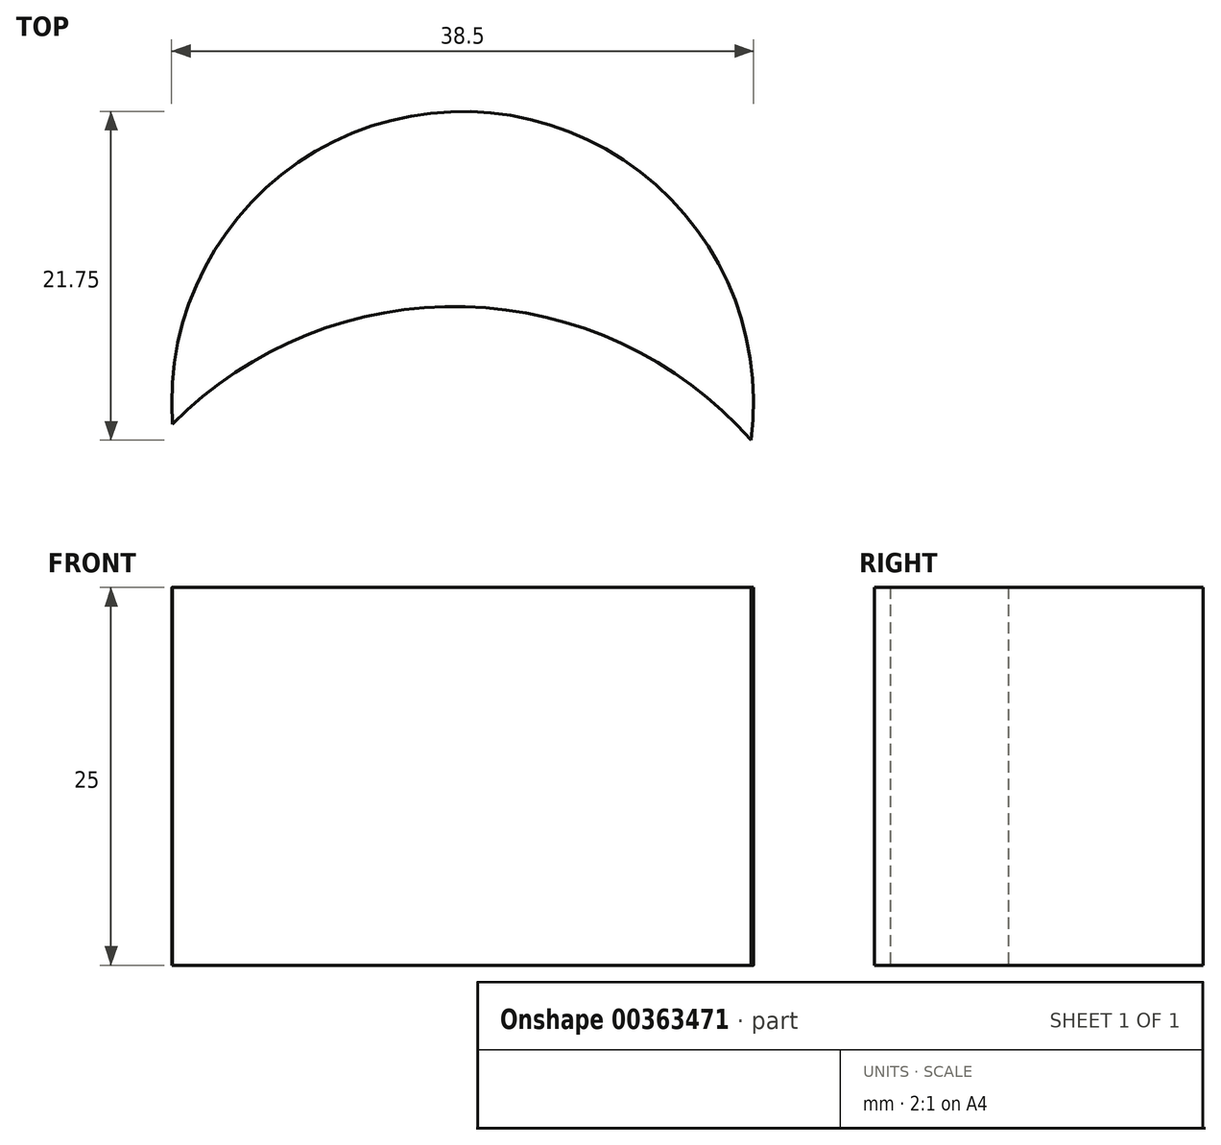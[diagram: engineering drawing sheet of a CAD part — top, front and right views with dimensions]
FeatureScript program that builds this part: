
annotation { "Feature Type Name" : "Feature", "Feature Type Description" : "" }
export const myFeature = defineFeature(function(context is Context, id is Id, definition is map)
    precondition{}
    {
        {
            var Q0;
            Q0=qCreatedBy(makeId("Top.planeOp"),FACE);
            var sketch = newSketch(context, id + "F0", { "sketchPlane" : qUnion([Q0])});
            skLineSegment(sketch, "E0", {"start": v(42.8, 55.87) * mm, "end": v(15.63, 55.87) * mm});
            skLineSegment(sketch, "E1", {"start": v(15.63, 55.87) * mm, "end": v(15.63, 21.62) * mm});
            skFitSpline(sketch, "E2", {"points": [v(53.37, -13.17) * mm, v(42.05, 30.73) * mm, v(24.39, 0) * mm, v(17.54, -7.23) * mm, v(-9.25, -11.18) * mm, v(-36.55, -37.18) * mm, v(-16.88, 21.62) * mm, v(15.63, 21.62) * mm], "startDerivative": vector(-49.45, 424.92) * mm, "endDerivative": vector(313.27, -121.77) * mm});
            skLineSegment(sketch, "E3", {"start": v(42.8, 55.87) * mm, "end": v(53.37, -13.17) * mm});
            skSolve(sketch);
        }
        {
            var Q0;
            Q0=qCreatedBy(makeId("Top.planeOp"),FACE);
            var sketch = newSketch(context, id + "F1", { "sketchPlane" : qUnion([Q0])});
            skCircle(sketch, "E4", {"center": v(-41.02, 68.2) * mm, "radius": 26.21 * mm});
            skCircle(sketch, "E5", {"center": v(-40.48, 88.06) * mm, "radius": 4.81 * mm});
            skCircle(sketch, "E6", {"center": v(-40.48, 88.06) * mm, "radius": 19.25 * mm});
            skCircle(sketch, "E7", {"center": v(-25.7, 0) * mm, "radius": 61.76 * mm});
            skSolve(sketch);
        }
        {
            var Q0;
            Q0 = qSketchRegion(id + "F1", true);
            var sketch = newSketch(context, id + "F2", { "sketchPlane" : qUnion([Q0])});
            skSolve(sketch);
        }
        {
            var Q0;
            {var subQ0=sQuery(id+"F1.wireOp",EDGE,"E6");var subQ1=sQuery(id+"F1.wireOp",EDGE,"E4");var subQ2=makeQuery(id+"F1.imprint","INTERSECT",VERTEX,{"disambiguationData":[OD(0.0)],"derivedFrom":[subQ1,subQ0]});Q0=makeQuery(id+"F2.imprint","IMPRINT",FACE,{"disambiguationData":[TD([[makeQuery(id+"F2.imprint","IMPRINT",EDGE,{"derivedFrom":makeQuery(id+"F1.imprint","IMPRINT",EDGE,{"disambiguationData":[TD([[subQ2,1.0]])],"derivedFrom":subQ1})}),-1.0]])]});}
            var Q1;
            {var subQ0=sQuery(id+"F1.wireOp",EDGE,"E7");var subQ1=sQuery(id+"F1.wireOp",EDGE,"E4");var subQ2=makeQuery(id+"F1.imprint","INTERSECT",VERTEX,{"disambiguationData":[OD(0.0)],"derivedFrom":[subQ1,subQ0]});Q1=makeQuery(id+"F2.imprint","IMPRINT",FACE,{"disambiguationData":[TD([[makeQuery(id+"F2.imprint","IMPRINT",EDGE,{"derivedFrom":makeQuery(id+"F1.imprint","IMPRINT",EDGE,{"disambiguationData":[TD([[subQ2,-1.0]])],"derivedFrom":subQ1})}),-1.0]])]});}
            var Q2;
            Q2=makeQuery(id+"F2.imprint","IMPRINT",FACE,{"disambiguationData":[TD([[makeQuery(id+"F2.imprint","IMPRINT",EDGE,{"derivedFrom":makeQuery(id+"F1.imprint","IMPRINT",EDGE,{"derivedFrom":sQuery(id+"F1.wireOp",EDGE,"E5")})}),-1.0]])]});
            extrude(context, id + "F3", {"entities" : qUnion([Q0, Q1, Q2]), "depth" : 25 * mm});
        }
        {
            var Q0;
            {var subQ0=sQuery(id+"F0.wireOp",EDGE,"E0");Q0=makeQuery(id+"F0.imprint","IMPRINT",FACE,{"disambiguationData":[TD([[makeQuery(id+"F0.imprint","IMPRINT",EDGE,{"derivedFrom":subQ0}),1.0]])]});}
            extrude(context, id + "F4", {"entities" : qUnion([Q0]), "operationType" : NewBodyOperationType.REMOVE, "endBound" : BoundingType.THROUGH_ALL, "depth" : 25 * mm});
        }
        {
            var Q0;
            Q0 = qSketchRegion(id + "F1", true);
            var sketch = newSketch(context, id + "F5", { "sketchPlane" : qUnion([Q0])});
            skEllipse(sketch, "E8", {"center": v(-53.44, 37.31) * mm, "majorRadius": 11.32 * mm, "minorRadius": 17.85 * mm, "majorAxis": v(-0.8, 0.6)});
            skSolve(sketch);
        }
        {
            var Q0;
            Q0 = qSketchRegion(id + "F5", true);
            var Q1;
            Q1=sQuery(id+"F5.wireOp",EDGE,"E8");
            extrude(context, id + "F6", {"entities" : qUnion([Q0]), "bodyType" : ToolBodyType.SURFACE, "operationType" : NewBodyOperationType.ADD, "surfaceEntities" : qUnion([Q1]), "oppositeDirection" : true, "depth" : 50 * mm});
        }
    });
